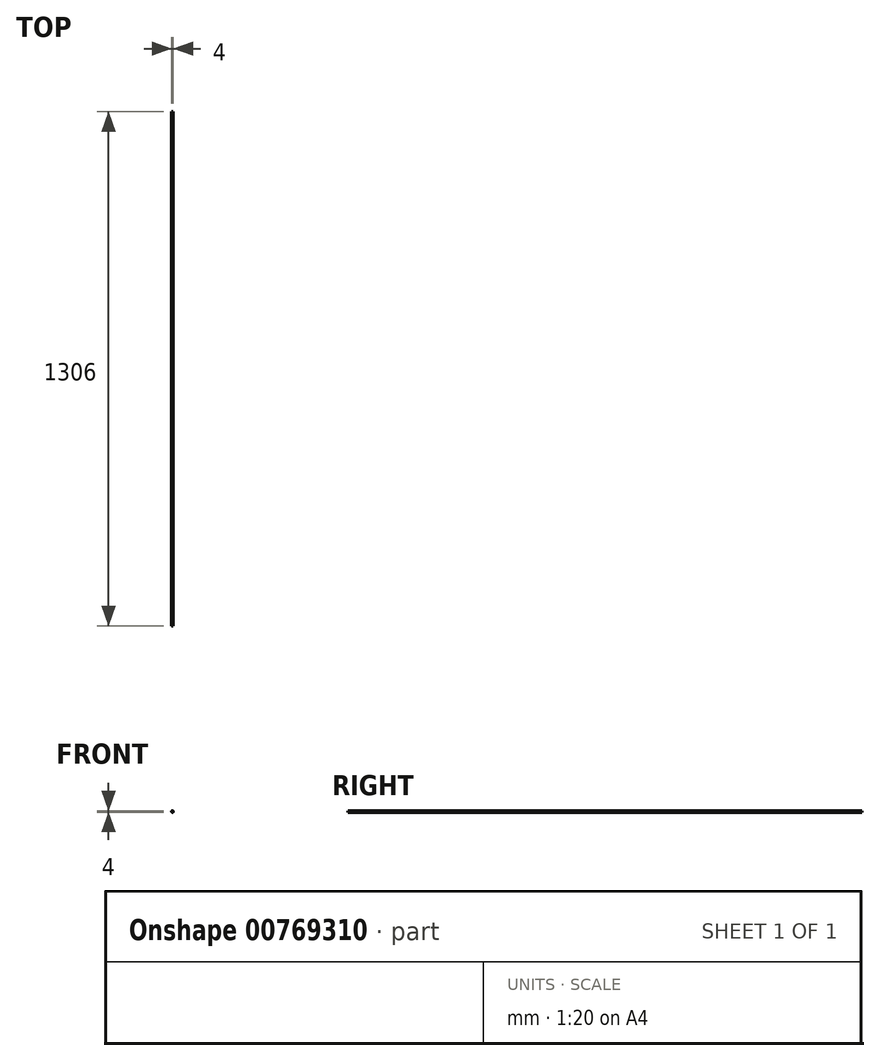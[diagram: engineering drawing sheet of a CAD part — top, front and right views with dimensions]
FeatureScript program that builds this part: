
annotation { "Feature Type Name" : "Feature", "Feature Type Description" : "" }
export const myFeature = defineFeature(function(context is Context, id is Id, definition is map)
    precondition{}
    {
        {
            var Q0;
            Q0=qCreatedBy(makeId("Front.planeOp"),FACE);
            var sketch = newSketch(context, id + "F0", { "sketchPlane" : qUnion([Q0])});
            skCircle(sketch, "E0", {"center": v(0, 0) * mm, "radius": 2 * mm});
            skSolve(sketch);
        }
        {
            var Q0;
            Q0=makeQuery(id+"F0.imprint","IMPRINT",FACE,{"disambiguationData":[TD([[makeQuery(id+"F0.imprint","IMPRINT",EDGE,{"derivedFrom":sQuery(id+"F0.wireOp",EDGE,"E0")}),1.0]])]});
            extrude(context, id + "F1", {"entities" : qUnion([Q0]), "depth" : 1306 * mm, "offsetDistance" : 25 * mm});
        }
    });
